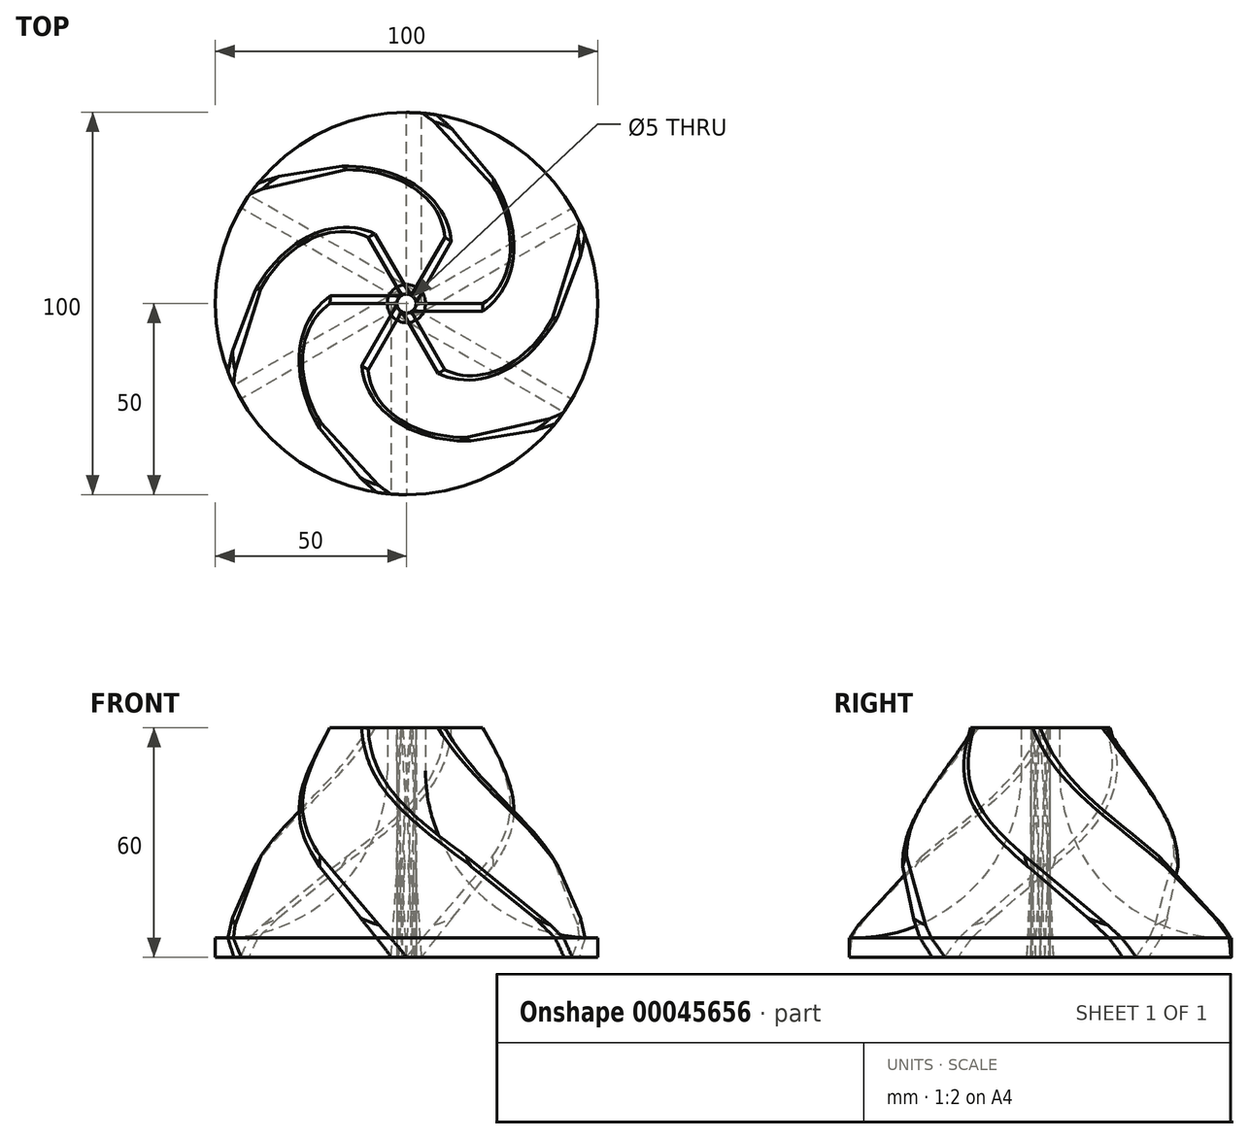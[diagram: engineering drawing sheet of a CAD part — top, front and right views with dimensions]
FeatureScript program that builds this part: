
annotation { "Feature Type Name" : "Feature", "Feature Type Description" : "" }
export const myFeature = defineFeature(function(context is Context, id is Id, definition is map)
    precondition{}
    {
        {
            var Q0;
            Q0=qCreatedBy(makeId("Front.planeOp"),FACE);
            var sketch = newSketch(context, id + "F0", { "sketchPlane" : qUnion([Q0])});
            skLineSegment(sketch, "E0", {"start": v(-50, 0) * mm, "end": v(0, 0) * mm});
            skLineSegment(sketch, "E1", {"start": v(0, 0) * mm, "end": v(0, 60) * mm});
            skLineSegment(sketch, "E2", {"start": v(0, 60) * mm, "end": v(-5, 60) * mm});
            skLineSegment(sketch, "E3", {"start": v(-50, 0) * mm, "end": v(-50, 5) * mm});
            skLineSegment(sketch, "E4", {"start": v(-5, 60) * mm, "end": v(-5, 48.72) * mm});
            skArc(sketch, "E5", {"start": v(-50, 5) * mm, "mid": v(-18.26, 17.35) * mm, "end": v(-5, 48.72) * mm});
            skSolve(sketch);
        }
        {
            var Q0;
            Q0 = qSketchRegion(id + "F0", true);
            var Q1;
            Q1=sQuery(id+"F0.wireOp",EDGE,"E1");
            revolve(context, id + "F1", {"entities" : qUnion([Q0]), "axis" : qUnion([Q1]), "revolveType" : RevolveType.FULL});
        }
        {
            var Q0;
            Q0=qCreatedBy(makeId("Top.planeOp"),FACE);
            var sketch = newSketch(context, id + "F2", { "sketchPlane" : qUnion([Q0])});
            skLineSegment(sketch, "E6", {"start": v(0, 0) * mm, "end": v(0, -55.38) * mm});
            skLineSegment(sketch, "E7.0", {"start": v(-4, 0) * mm, "end": v(-4, -55.38) * mm});
            skLineSegment(sketch, "E8", {"start": v(0, -55.38) * mm, "end": v(-4, -55.38) * mm});
            skLineSegment(sketch, "E9", {"start": v(0, 0) * mm, "end": v(-4, 0) * mm});
            skSolve(sketch);
        }
        {
            var Q0;
            Q0=qCreatedBy(makeId("Top.planeOp"),FACE);
            cPlane(context, id + "F3", {"entities" : qUnion([Q0]), "cplaneType" : CPlaneType.OFFSET, "offset" : 60 * mm, "width" : 150 * mm, "height" : 150 * mm});
        }
        {
            var Q0;
            Q0=qCreatedBy(id+"F3.planeOp",FACE);
            var sketch = newSketch(context, id + "F4", { "sketchPlane" : qUnion([Q0])});
            skLineSegment(sketch, "E10", {"start": v(0, 0) * mm, "end": v(-51.21, 0) * mm});
            skLineSegment(sketch, "E11.0", {"start": v(0, 2) * mm, "end": v(-51.21, 2) * mm});
            skLineSegment(sketch, "E12", {"start": v(0, 0) * mm, "end": v(0, 2) * mm});
            skLineSegment(sketch, "E13", {"start": v(-51.21, 0) * mm, "end": v(-51.21, 2) * mm});
            skSolve(sketch);
        }
        {
            var Q1;
            Q1 = qSketchRegion(id + "F2", true);
            var Q2;
            Q2 = qSketchRegion(id + "F4", true);
            loft(context, id + "F5", {"sheetProfilesArray" : [{ "sheetProfileEntities" : qUnion([Q1]) }, { "sheetProfileEntities" : qUnion([Q2]) }], "trimGuidesByProfiles" : true});
        }
        {
            var Q0;
            Q0=qCreatedBy(makeId("Front.planeOp"),FACE);
            var sketch = newSketch(context, id + "F6", { "sketchPlane" : qUnion([Q0])});
            skLineSegment(sketch, "E14", {"start": v(-50, 5) * mm, "end": v(-20, 60) * mm});
            skLineSegment(sketch, "E15", {"start": v(-20, 60) * mm, "end": v(-70.23, 60) * mm});
            skLineSegment(sketch, "E16", {"start": v(-70.23, 60) * mm, "end": v(-70.23, 0) * mm});
            skLineSegment(sketch, "E17", {"start": v(-70.23, 0) * mm, "end": v(-50, 0) * mm});
            skLineSegment(sketch, "E18", {"start": v(-50, 0) * mm, "end": v(-50, 5) * mm});
            skLineSegment(sketch, "E19", {"start": v(0, 0) * mm, "end": v(0, 70.03) * mm, "construction": true});
            skSolve(sketch);
        }
        {
            var Q0;
            Q0=qCreatedBy(makeId("Front.planeOp"),FACE);
            var sketch = newSketch(context, id + "F7", { "sketchPlane" : qUnion([Q0])});
            skLineSegment(sketch, "E20", {"start": v(0, -41.83) * mm, "end": v(0, 70.25) * mm, "construction": true});
            skSolve(sketch);
        }
        {
            var Q0;
            Q0=makeQuery(id+"F5.opLoft","SWEPT_BODY",BODY,{"disambiguationData":[OSD([makeQuery(id+"F2.imprint","IMPRINT",FACE,{"disambiguationData":[TD([[makeQuery(id+"F2.imprint","IMPRINT",EDGE,{"derivedFrom":sQuery(id+"F2.wireOp",EDGE,"E6")}),-1.0]])]}),makeQuery(id+"F4.imprint","IMPRINT",FACE,{"disambiguationData":[TD([[makeQuery(id+"F4.imprint","IMPRINT",EDGE,{"derivedFrom":sQuery(id+"F4.wireOp",EDGE,"E10")}),-1.0]])]})])]});
            var Q1;
            Q1=sQuery(id+"F7.wireOp",EDGE,"E20");
            circularPattern(context, id + "F8", {"entities" : qUnion([Q0]), "axis" : qUnion([Q1]), "angle" : 60 * degree, "instanceCount" : 6, "fullFeaturePattern" : false});
        }
        {
            var Q0;
            Q0 = qSketchRegion(id + "F6", true);
            var Q1;
            Q1=sQuery(id+"F6.wireOp",EDGE,"E19");
            revolve(context, id + "F9", {"operationType" : NewBodyOperationType.REMOVE, "surfaceOperationType" : NewSurfaceOperationType.NEW, "entities" : qUnion([Q0]), "axis" : qUnion([Q1]), "revolveType" : RevolveType.FULL, "oppositeDirection" : true});
        }
        {
            var Q0;
            Q0=qCreatedBy(makeId("Top.planeOp"),FACE);
            var sketch = newSketch(context, id + "F10", { "sketchPlane" : qUnion([Q0])});
            skCircle(sketch, "E21", {"center": v(0, 0) * mm, "radius": 2.5 * mm});
            skSolve(sketch);
        }
        {
            var Q0;
            Q0 = qSketchRegion(id + "F10", true);
            extrude(context, id + "F11", {"entities" : qUnion([Q0]), "operationType" : NewBodyOperationType.REMOVE, "endBound" : BoundingType.THROUGH_ALL, "depth" : 25 * mm});
        }
    });
